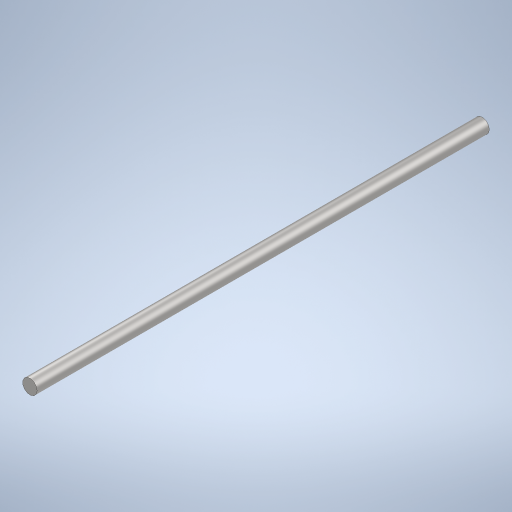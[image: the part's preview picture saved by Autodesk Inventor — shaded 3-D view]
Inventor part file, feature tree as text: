
AUTODESK INVENTOR PART (.ipt)
format: ipt  version: 2023.2 (Build 272271000, 271)  size: 258,560 bytes
history: native  units: mm
features: extrude x1, sketch x1
ambient origin geometry x8: Origin, YZ Plane, XZ Plane, XY Plane, X Axis, Y Axis, Z Axis, Center Point
bodies: Solid1 (feature_tree)
feature tree (2):
  extrude  "Extrusion1"  Depth=250.0mm TaperAngle=0.0deg
  sketch  "Sketch1"  dims[d0=8.0mm d1=250.0mm d2=0.0mm]
